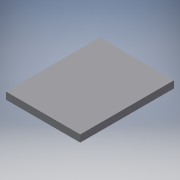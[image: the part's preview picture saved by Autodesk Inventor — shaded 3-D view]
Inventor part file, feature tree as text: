
AUTODESK INVENTOR PART (.ipt)
format: ipt  version: 2016 (Build 200138000, 138)  size: 111,104 bytes
history: native  units: mm
features: extrude x2, sketch x2, fillet x1
ambient origin geometry x8: Origin, YZ Plane, XZ Plane, XY Plane, X Axis, Y Axis, Z Axis, Center Point
bodies: Solid1 (feature_tree)
feature tree (5):
  extrude  "Extrusion1"  Depth=95.0mm
  extrude  "Extrusion3"  Depth=7.0mm
  fillet  "Fillet1"  Radius=35.0mm
  sketch  "Sketch1"  dims[d0=120.0mm d1=95.0mm]
  sketch  "Sketch3"  dims[d2=6.0mm d3=0.0mm d9=7.0mm d10=35.0mm d11=75.0mm d12=3.0mm d13=0.0mm d14=7.0mm]
